FCSTD DOCUMENT  (FreeCAD 1.0R38641 +468 (Git))
Label: Base
License: All rights reserved
LicenseURL: https://en.wikipedia.org/wiki/All_rights_reserved
objects: App::Link×2, App::FeaturePython×1, Assembly::JointGroup×1, Assembly::AssemblyObject×1, App::Part×1
EXTERNAL_REF file=B1.FCStd obj=B003
EXTERNAL_REF file=B2.FCStd obj=B004

FEATURE [App::Link] B003
  LinkedObject = -> <external B1.FCStd>#B003
FEATURE [App::FeaturePython] GroundedJoint  # Assembly grounded joint (typed FeaturePython)
  ObjectToGround = -> B003
FEATURE [Assembly::JointGroup] Joints
  Group = -> [GroundedJoint]
FEATURE [App::Link] B004
  LinkedObject = -> <external B2.FCStd>#B004
FEATURE [Assembly::AssemblyObject] Assembly
  Group = -> [Joints,B003,GroundedJoint,B004]
  Origin = -> Origin
  Placement = pos=(190.3,0.1,180.2) rot=(0,0,1;0rad)
  Type = Assembly
FEATURE [App::Part] Part
  Group = -> [Assembly]
  Origin = -> Origin001
  Placement = pos=(0,-2.3e-15,-0.05) rot=(-1,0,0;4.71239rad)

RESOLVED EXTERNAL PARTS (link-assembly join: the EXTERNAL_REF files above that resolve inside this repo's crawl, each included once):
---- part B1.FCStd = doc fcstd_58c6a62270fd ----
FCSTD DOCUMENT  (FreeCAD 1.0R38641 +468 (Git))
Label: B1
License: All rights reserved
LicenseURL: https://en.wikipedia.org/wiki/All_rights_reserved
objects: Part::Feature×1, Part::Refine×1
note: 2 computed .brp shape members not serialized (recipe doc carries the construction recipe); baked Part::Feature solids carry a one-line shape summary decoded from their .brp

FEATURE [Part::Feature] B002
  shape: bbox 89.5 x 52.5 x 44.75 mm, 4736 faces, 0 solids (baked)
FEATURE [Part::Refine] B003
  Source = -> B002
---- part B2.FCStd = doc fcstd_a5884823b3fd ----
FCSTD DOCUMENT  (FreeCAD 1.0R38641 +468 (Git))
Label: B2
License: All rights reserved
LicenseURL: https://en.wikipedia.org/wiki/All_rights_reserved
objects: Part::Feature×1, Part::Refine×1
note: 2 computed .brp shape members not serialized (recipe doc carries the construction recipe); baked Part::Feature solids carry a one-line shape summary decoded from their .brp

FEATURE [Part::Feature] B003
  shape: bbox 89.5 x 52.5 x 44.75 mm, 3732 faces, 0 solids (baked)
FEATURE [Part::Refine] B004
  Source = -> B003
